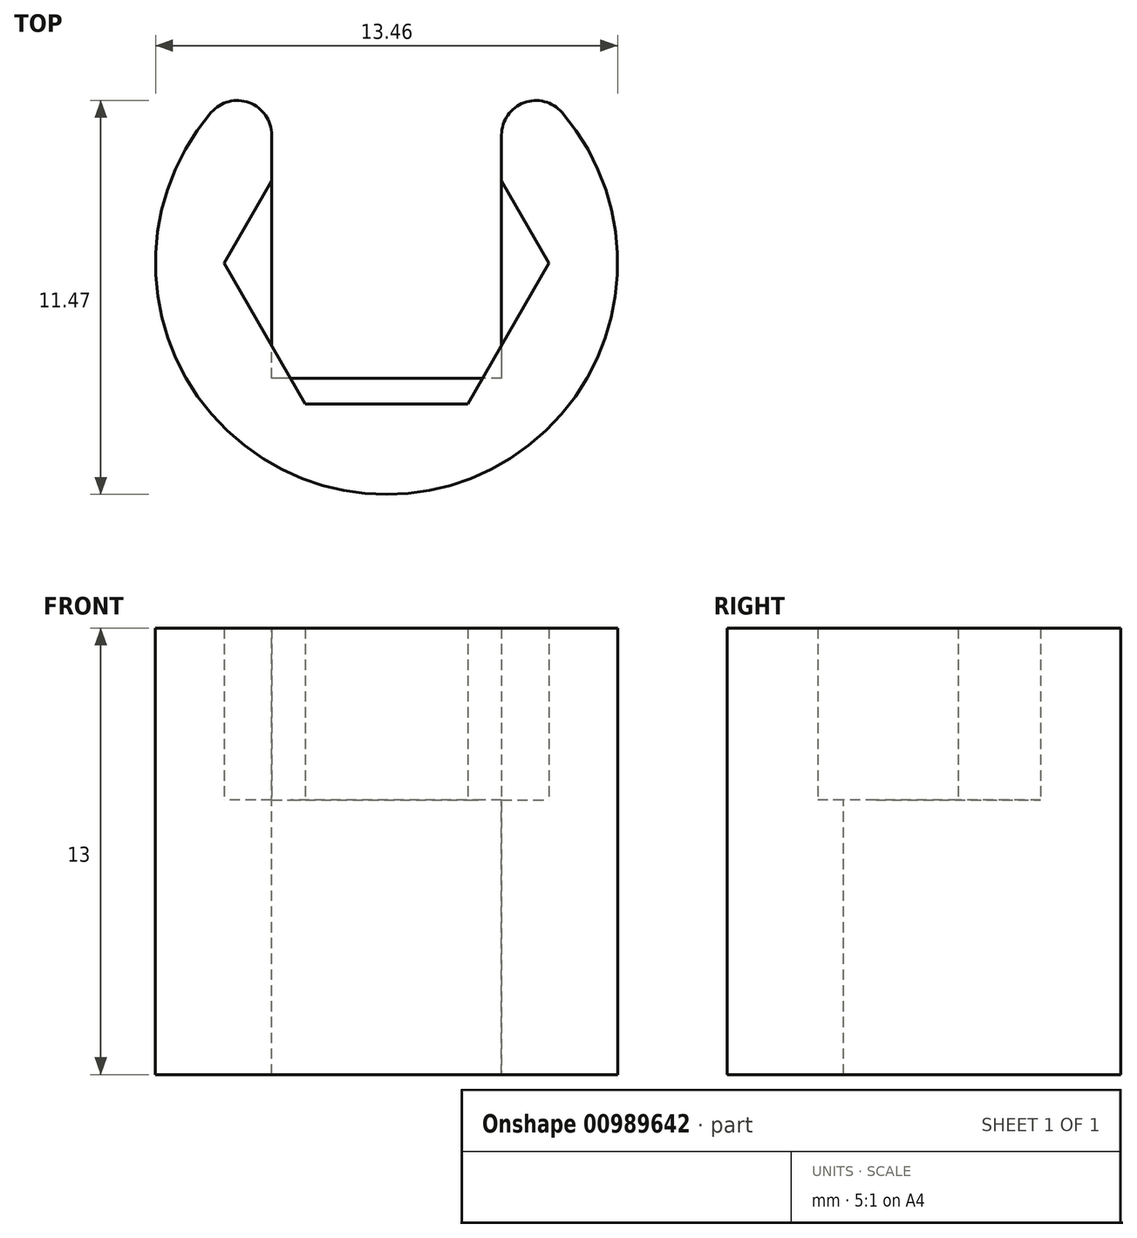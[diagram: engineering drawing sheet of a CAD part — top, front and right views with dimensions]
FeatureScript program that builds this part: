
annotation { "Feature Type Name" : "Feature", "Feature Type Description" : "" }
export const myFeature = defineFeature(function(context is Context, id is Id, definition is map)
    precondition{}
    {
        {
            var Q0;
            Q0=qCreatedBy(makeId("Top.planeOp"),FACE);
            var sketch = newSketch(context, id + "F0", { "sketchPlane" : qUnion([Q0])});
            skCircle(sketch, "E0.cCircle", {"center": v(0, 0) * mm, "radius": 4.1 * mm, "construction": true});
            skLineSegment(sketch, "E0.0", {"start": v(-2.37, 4.1) * mm, "end": v(2.37, 4.1) * mm});
            skLineSegment(sketch, "E0.1", {"start": v(2.37, 4.1) * mm, "end": v(4.73, 0) * mm});
            skLineSegment(sketch, "E0.2", {"start": v(4.73, 0) * mm, "end": v(2.37, -4.1) * mm});
            skLineSegment(sketch, "E0.3", {"start": v(2.37, -4.1) * mm, "end": v(-2.37, -4.1) * mm});
            skLineSegment(sketch, "E0.4", {"start": v(-2.37, -4.1) * mm, "end": v(-4.73, 0) * mm});
            skLineSegment(sketch, "E0.5", {"start": v(-4.73, 0) * mm, "end": v(-2.37, 4.1) * mm});
            skPoint(sketch, "E0.0.midPoint", {"position": v(0, 4.1) * mm});
            skCircle(sketch, "E1", {"center": v(0, 0) * mm, "radius": 6.73 * mm});
            skLineSegment(sketch, "E2", {"start": v(-3.35, -2.4) * mm, "end": v(-3.35, -5.84) * mm});
            skLineSegment(sketch, "E3", {"start": v(3.35, -2.4) * mm, "end": v(3.35, -5.84) * mm});
            skSolve(sketch);
        }
        {
            var Q0;
            {var subQ4=sQuery(id+"F0.wireOp",EDGE,"E0.0");Q0=makeQuery(id+"F0.imprint","IMPRINT",FACE,{"disambiguationData":[TD([[makeQuery(id+"F0.imprint","IMPRINT",EDGE,{"derivedFrom":subQ4}),1.0]])]});}
            extrude(context, id + "F1", {"entities" : qUnion([Q0]), "oppositeDirection" : true, "depth" : 5 * mm, "offsetDistance" : 25 * mm});
        }
        {
            var Q0;
            Q0=qCreatedBy(makeId("Top.planeOp"),FACE);
            var sketch = newSketch(context, id + "F2", { "sketchPlane" : qUnion([Q0])});
            skLineSegment(sketch, "E4.bottom", {"start": v(3.35, -3.35) * mm, "end": v(-3.35, -3.35) * mm});
            skLineSegment(sketch, "E4.top", {"start": v(3.35, 3.35) * mm, "end": v(-3.35, 3.35) * mm});
            skLineSegment(sketch, "E4.left", {"start": v(3.35, -3.35) * mm, "end": v(3.35, 3.35) * mm});
            skLineSegment(sketch, "E4.right", {"start": v(-3.35, -3.35) * mm, "end": v(-3.35, 3.35) * mm});
            skPoint(sketch, "E4.middle", {"position": v(0, 0) * mm});
            skCircle(sketch, "E5", {"center": v(0, 0) * mm, "radius": 6.73 * mm});
            skLineSegment(sketch, "E6", {"start": v(3.35, -3.35) * mm, "end": v(3.35, -5.84) * mm});
            skLineSegment(sketch, "E7", {"start": v(-3.35, -3.35) * mm, "end": v(-3.35, -5.84) * mm});
            skSolve(sketch);
        }
        {
            var Q0;
            Q0=makeQuery(id+"F2.imprint","IMPRINT",FACE,{"disambiguationData":[TD([[makeQuery(id+"F2.imprint","IMPRINT",EDGE,{"derivedFrom":sQuery(id+"F2.wireOp",EDGE,"E4.top")}),-1.0]])]});
            extrude(context, id + "F3", {"entities" : qUnion([Q0]), "operationType" : NewBodyOperationType.ADD, "depth" : 8 * mm, "offsetDistance" : 25 * mm});
        }
        {
            var Q0;
            Q0=makeQuery(id+"F3.boolean.opBoolean","MERGE",EDGE,{"derivedFrom":[makeQuery(id+"F1.opExtrude","SWEPT_EDGE",EDGE,{"disambiguationData":[OSD([sQuery(id+"F0.wireOp",EDGE,"E1"),sQuery(id+"F0.wireOp",EDGE,"15atYexw-wkGi-RGVK-VieP-IfGARjfFSvEx")])]}),makeQuery(id+"F3.opExtrude","SWEPT_EDGE",EDGE,{"disambiguationData":[OSD([sQuery(id+"F2.wireOp",EDGE,"E5"),sQuery(id+"F2.wireOp",EDGE,"E8P2wMtW-PEIw-0eHr-0TBw-t3urmAJEjyys")])]})]});
            var Q1;
            Q1=makeQuery(id+"F3.boolean.opBoolean","MERGE",EDGE,{"derivedFrom":[makeQuery(id+"F1.opExtrude","SWEPT_EDGE",EDGE,{"disambiguationData":[OSD([sQuery(id+"F0.wireOp",EDGE,"E1"),sQuery(id+"F0.wireOp",EDGE,"4eqVKCV7-gGIA-hiSL-akk3-MKtsuxVcPMcF")])]}),makeQuery(id+"F3.opExtrude","SWEPT_EDGE",EDGE,{"disambiguationData":[OSD([sQuery(id+"F2.wireOp",EDGE,"E5"),sQuery(id+"F2.wireOp",EDGE,"08yGTR1c-zWFU-57NL-uUrG-9kw9fsxUXKZp")])]})]});
            fillet(context, id + "F4", {"entities" : qUnion([Q0, Q1]), "tangentPropagation" : true, "radius" : 1 * mm, "defaultsChanged" : true, "vertexSettings" : [], "allowEdgeOverflow" : false});
        }
        {
            var Q0;
            Q0=makeQuery(id+"F1.opExtrude","SWEPT_BODY",BODY,{"disambiguationData":[OSD([sQuery(id+"F0.wireOp",EDGE,"E0.0"),sQuery(id+"F0.wireOp",EDGE,"E0.1"),sQuery(id+"F0.wireOp",EDGE,"E0.2"),sQuery(id+"F0.wireOp",EDGE,"E0.3"),sQuery(id+"F0.wireOp",EDGE,"E0.4"),sQuery(id+"F0.wireOp",EDGE,"E0.5"),sQuery(id+"F0.wireOp",EDGE,"E1"),sQuery(id+"F0.wireOp",EDGE,"15atYexw-wkGi-RGVK-VieP-IfGARjfFSvEx"),sQuery(id+"F0.wireOp",EDGE,"4eqVKCV7-gGIA-hiSL-akk3-MKtsuxVcPMcF")])]});
            var Q1;
            Q1=makeQuery(id+"F3.opExtrude","CAP_EDGE",EDGE,{"disambiguationData":[OSD([sQuery(id+"F2.wireOp",EDGE,"E4.top")])],"isStart":false});
            transform(context, id + "F5", {"entities" : qUnion([Q0]), "transformType" : TransformType.ROTATION, "transformAxis" : qUnion([Q1]), "angle" : 180 * degree, "makeCopy" : false});
        }
    });
